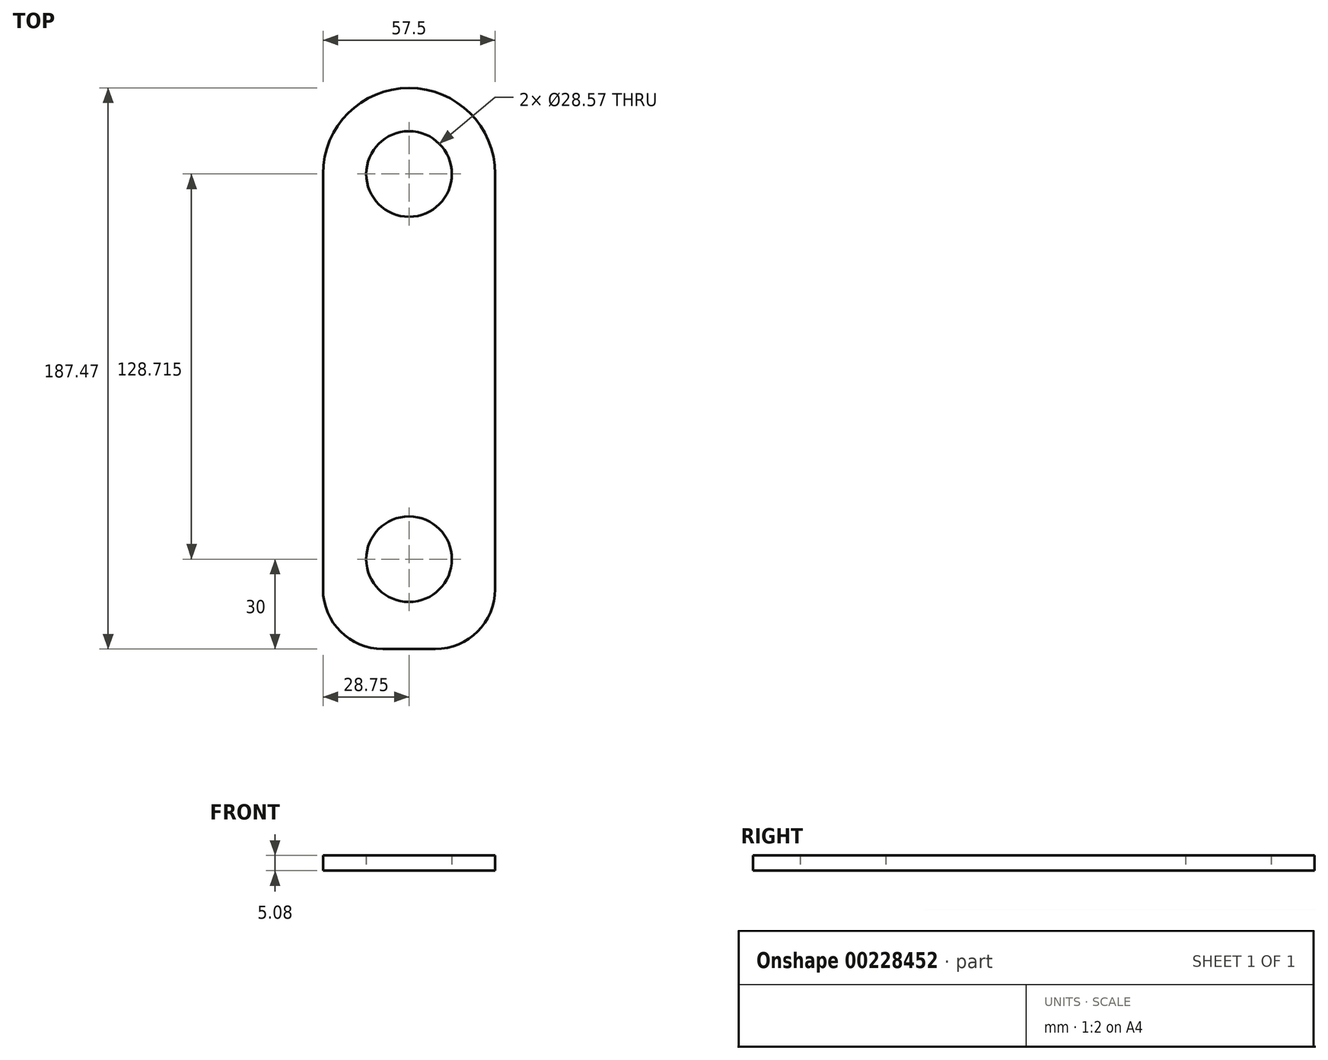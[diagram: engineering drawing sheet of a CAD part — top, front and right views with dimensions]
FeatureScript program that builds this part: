
annotation { "Feature Type Name" : "Feature", "Feature Type Description" : "" }
export const myFeature = defineFeature(function(context is Context, id is Id, definition is map)
    precondition{}
    {
        {
            var Q0;
            Q0=qCreatedBy(makeId("Top.planeOp"),FACE);
            var sketch = newSketch(context, id + "F0", { "sketchPlane" : qUnion([Q0])});
            skLineSegment(sketch, "E0.bottom", {"start": v(20, 0) * mm, "end": v(37.5, 0) * mm});
            skLineSegment(sketch, "E0.left", {"start": v(0, 20) * mm, "end": v(0, 158.72) * mm});
            skLineSegment(sketch, "E0.right", {"start": v(57.5, 20) * mm, "end": v(57.5, 158.72) * mm});
            skArc(sketch, "E1", {"start": v(57.5, 158.72) * mm, "mid": v(28.75, 187.47) * mm, "end": v(0, 158.72) * mm});
            skCircle(sketch, "E2", {"center": v(28.75, 158.72) * mm, "radius": 14.29 * mm});
            skCircle(sketch, "E3", {"center": v(28.75, 30) * mm, "radius": 14.29 * mm});
            skPoint(sketch, "E4.visualSharp", {"position": v(0, 0) * mm});
            skArc(sketch, "E4.filletArc", {"start": v(0, 20) * mm, "mid": v(5.86, 5.86) * mm, "end": v(20, 0) * mm});
            skPoint(sketch, "E5.visualSharp", {"position": v(57.5, 0) * mm});
            skArc(sketch, "E5.filletArc", {"start": v(37.5, 0) * mm, "mid": v(51.64, 5.86) * mm, "end": v(57.5, 20) * mm});
            skSolve(sketch);
        }
        {
            var Q0;
            {var subQ1=sQuery(id+"F0.wireOp",EDGE,"E0.top");Q0=makeQuery(id+"F0.imprint","IMPRINT",FACE,{"disambiguationData":[TD([[makeQuery(id+"F0.imprint","IMPRINT",EDGE,{"derivedFrom":subQ1}),-1.0]])]});}
            var Q1;
            Q1=makeQuery(id+"F0.imprint","IMPRINT",FACE,{"disambiguationData":[TD([[makeQuery(id+"F0.imprint","IMPRINT",EDGE,{"derivedFrom":sQuery(id+"F0.wireOp",EDGE,"E0.bottom")}),1.0]])]});
            extrude(context, id + "F1", {"entities" : qUnion([Q0, Q1]), "depth" : 5.08 * mm});
        }
    });
